# Revit family: Handrail_Colonial
name_source: partatom
category: Profiles
units: mm (PartAtom-declared; Revit-internal decimal feet)

## family parameters
Classification Number = 23.30.80.14
Profile Usage = <Generic>
Rotate with component = No
Section Shape = Not Defined

## types (3) — shared parameters
Assembly Code = C2020300
Construction Details = http://www.arcat.com
Description = Handrail
Expected Lifespan (Years) = 50
Green Building-LEED = http://www.arcat.com
Keynote = 06430
Maintenance Schedule (Months) = 24
Manufacturer = Generic
Manufacturer Fax = (203) 939-2444
Manufacturer Website = http://www.arcat.com
Model = Generic
Product Data = http://www.arcat.com
Product Properties = http://www.arcat.com
Rail Height = 0' - 2"
Specification = http://www.arcat.com
Warranty Duration (Years) = 1

## per-type parameters (varying)
| type | Railing Width | rlctr |
| 2-7/8" x 2" | 0' - 2 7/8" | 0' - 1 5/8" |
| 1-7/8" x 2" | 0' - 1 7/8" | 0' - 0 5/8" |
| 2 1/4" x 2" | 0' - 2 1/4" | 0' - 1" |
